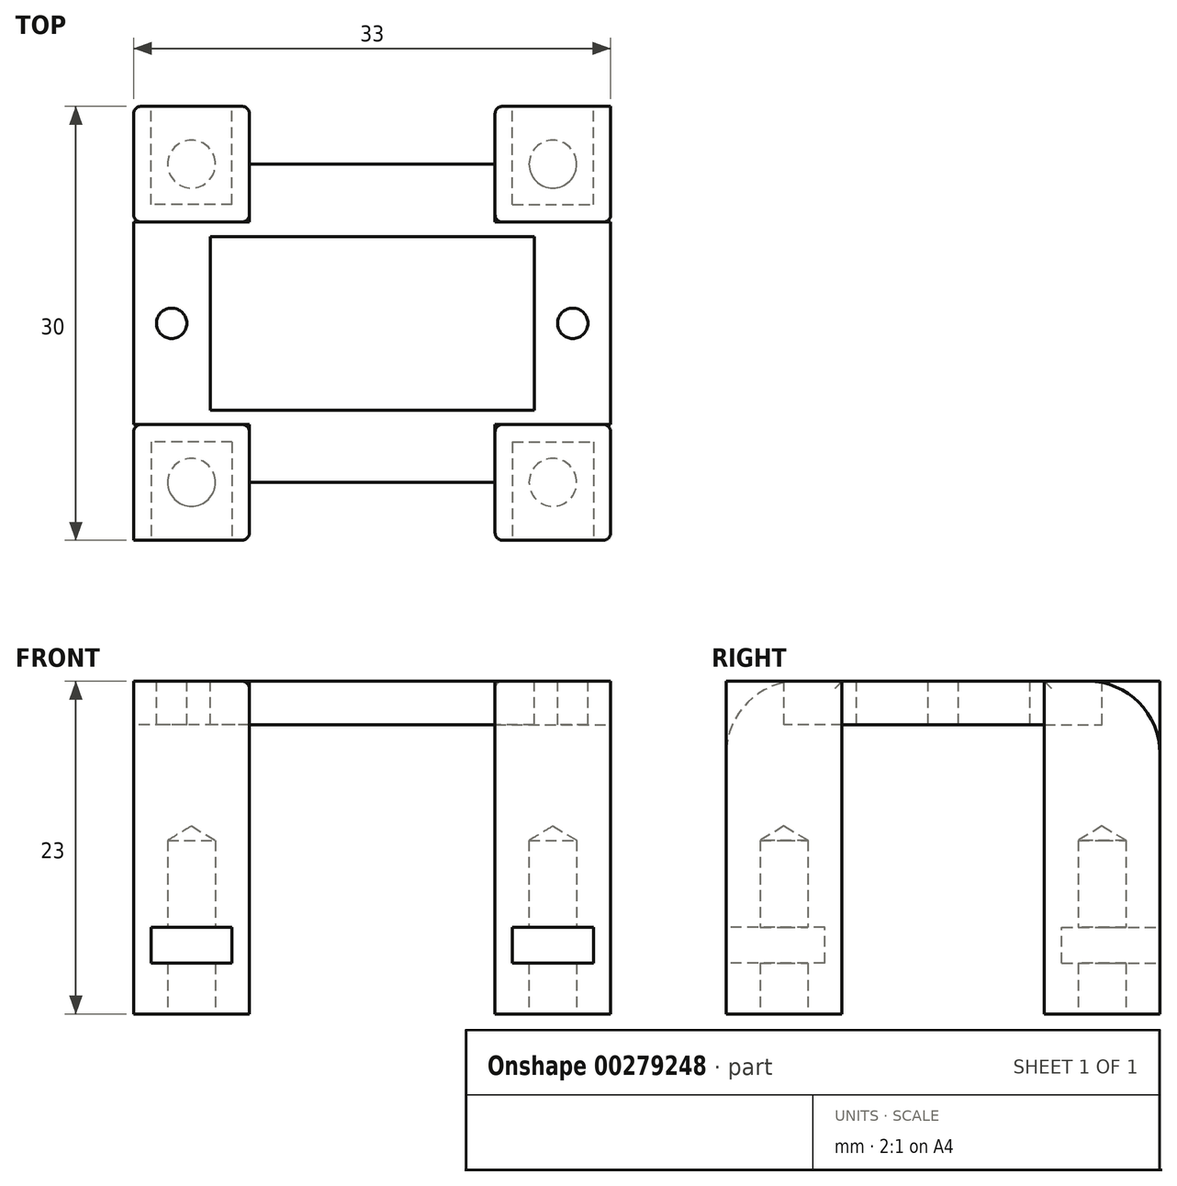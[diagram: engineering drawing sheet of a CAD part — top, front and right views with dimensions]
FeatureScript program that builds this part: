
annotation { "Feature Type Name" : "Feature", "Feature Type Description" : "" }
export const myFeature = defineFeature(function(context is Context, id is Id, definition is map)
    precondition{}
    {
        {
            var Q0;
            Q0=qCreatedBy(makeId("Top.planeOp"),FACE);
            var sketch = newSketch(context, id + "F0", { "sketchPlane" : qUnion([Q0])});
            skLineSegment(sketch, "E0.bottom", {"start": v(11.2, -6) * mm, "end": v(-11.2, -6) * mm});
            skLineSegment(sketch, "E0.top", {"start": v(11.2, 6) * mm, "end": v(-11.2, 6) * mm});
            skLineSegment(sketch, "E0.left", {"start": v(11.2, -6) * mm, "end": v(11.2, 6) * mm});
            skLineSegment(sketch, "E0.right", {"start": v(-11.2, -6) * mm, "end": v(-11.2, 6) * mm});
            skPoint(sketch, "E0.middle", {"position": v(0, 0) * mm});
            skLineSegment(sketch, "E1.bottom", {"start": v(16.5, -11) * mm, "end": v(-16.5, -11) * mm});
            skLineSegment(sketch, "E1.top", {"start": v(16.5, 11) * mm, "end": v(-16.5, 11) * mm});
            skLineSegment(sketch, "E1.left", {"start": v(16.5, -11) * mm, "end": v(16.5, 11) * mm});
            skLineSegment(sketch, "E1.right", {"start": v(-16.5, -11) * mm, "end": v(-16.5, 11) * mm});
            skCircle(sketch, "E2", {"center": v(-13.88, 0) * mm, "radius": 1.05 * mm});
            skCircle(sketch, "E3.MirrorC", {"center": v(13.88, 0) * mm, "radius": 1.05 * mm});
            skCircle(sketch, "E4", {"center": v(-12.5, 11) * mm, "radius": 1.57 * mm});
            skLineSegment(sketch, "E5.bottom", {"start": v(-8.5, 7) * mm, "end": v(-16.5, 7) * mm});
            skLineSegment(sketch, "E5.top", {"start": v(-8.5, 15) * mm, "end": v(-16.5, 15) * mm});
            skLineSegment(sketch, "E5.left", {"start": v(-8.5, 7) * mm, "end": v(-8.5, 15) * mm});
            skLineSegment(sketch, "E5.right", {"start": v(-16.5, 7) * mm, "end": v(-16.5, 15) * mm});
            skLineSegment(sketch, "E6.MirrorCS", {"start": v(16.5, 7) * mm, "end": v(16.5, 15) * mm});
            skLineSegment(sketch, "E7.MirrorCS", {"start": v(8.5, 7) * mm, "end": v(8.5, 15) * mm});
            skLineSegment(sketch, "E8.MirrorCS", {"start": v(8.5, 7) * mm, "end": v(16.5, 7) * mm});
            skLineSegment(sketch, "E9.MirrorCS", {"start": v(8.5, 15) * mm, "end": v(16.5, 15) * mm});
            skCircle(sketch, "E10.MirrorC", {"center": v(12.5, 11) * mm, "radius": 1.57 * mm});
            skLineSegment(sketch, "E11.MirrorCS", {"start": v(16.5, -7) * mm, "end": v(16.5, -15) * mm});
            skLineSegment(sketch, "E12.MirrorCS", {"start": v(8.5, -7) * mm, "end": v(16.5, -7) * mm});
            skLineSegment(sketch, "E13.MirrorCS", {"start": v(8.5, -15) * mm, "end": v(16.5, -15) * mm});
            skLineSegment(sketch, "E14.MirrorCS", {"start": v(8.5, -7) * mm, "end": v(8.5, -15) * mm});
            skCircle(sketch, "E15.MirrorC", {"center": v(12.5, -11) * mm, "radius": 1.57 * mm});
            skCircle(sketch, "E16.MirrorC", {"center": v(-12.5, -11) * mm, "radius": 1.57 * mm});
            skLineSegment(sketch, "E17.MirrorCS", {"start": v(-8.5, -7) * mm, "end": v(-16.5, -7) * mm});
            skLineSegment(sketch, "E18.MirrorCS", {"start": v(-8.5, -7) * mm, "end": v(-8.5, -15) * mm});
            skLineSegment(sketch, "E19.MirrorCS", {"start": v(-8.5, -15) * mm, "end": v(-16.5, -15) * mm});
            skLineSegment(sketch, "E20.MirrorCS", {"start": v(-16.5, -7) * mm, "end": v(-16.5, -15) * mm});
            skSolve(sketch);
        }
        {
            var Q0;
            {var subQ6=sQuery(id+"F0.wireOp",EDGE,"E5.top");Q0=makeQuery(id+"F0.imprint","IMPRINT",FACE,{"disambiguationData":[TD([[makeQuery(id+"F0.imprint","IMPRINT",EDGE,{"derivedFrom":subQ6}),1.0]])]});}
            var Q1;
            {var subQ0=sQuery(id+"F0.wireOp",EDGE,"E4");var subQ1=sQuery(id+"F0.wireOp",EDGE,"E1.top");var subQ2=makeQuery(id+"F0.imprint","INTERSECT",VERTEX,{"disambiguationData":[OD(0.0)],"derivedFrom":[subQ1,subQ0]});Q1=makeQuery(id+"F0.imprint","IMPRINT",FACE,{"disambiguationData":[TD([[makeQuery(id+"F0.imprint","IMPRINT",EDGE,{"disambiguationData":[TD([[subQ2,-1.0]])],"derivedFrom":subQ1}),-1.0]])]});}
            var Q2;
            {var subQ0=sQuery(id+"F0.wireOp",EDGE,"E4");var subQ1=sQuery(id+"F0.wireOp",EDGE,"E1.top");var subQ2=makeQuery(id+"F0.imprint","INTERSECT",VERTEX,{"disambiguationData":[OD(0.0)],"derivedFrom":[subQ1,subQ0]});Q2=makeQuery(id+"F0.imprint","IMPRINT",FACE,{"disambiguationData":[TD([[makeQuery(id+"F0.imprint","IMPRINT",EDGE,{"disambiguationData":[TD([[subQ2,-1.0]])],"derivedFrom":subQ1}),1.0]])]});}
            var Q3;
            {var subQ0=sQuery(id+"F0.wireOp",EDGE,"E5.bottom");Q3=makeQuery(id+"F0.imprint","IMPRINT",FACE,{"disambiguationData":[TD([[makeQuery(id+"F0.imprint","IMPRINT",EDGE,{"derivedFrom":subQ0}),-1.0]])]});}
            var Q4;
            {var subQ0=sQuery(id+"F0.wireOp",EDGE,"E9.MirrorCS");Q4=makeQuery(id+"F0.imprint","IMPRINT",FACE,{"disambiguationData":[TD([[makeQuery(id+"F0.imprint","IMPRINT",EDGE,{"derivedFrom":subQ0}),-1.0]])]});}
            var Q5;
            {var subQ0=sQuery(id+"F0.wireOp",EDGE,"E10.MirrorC");var subQ1=sQuery(id+"F0.wireOp",EDGE,"E1.top");var subQ2=makeQuery(id+"F0.imprint","INTERSECT",VERTEX,{"disambiguationData":[OD(0.0)],"derivedFrom":[subQ1,subQ0]});Q5=makeQuery(id+"F0.imprint","IMPRINT",FACE,{"disambiguationData":[TD([[makeQuery(id+"F0.imprint","IMPRINT",EDGE,{"disambiguationData":[TD([[subQ2,-1.0]])],"derivedFrom":subQ1}),-1.0]])]});}
            var Q6;
            {var subQ0=sQuery(id+"F0.wireOp",EDGE,"E10.MirrorC");var subQ1=sQuery(id+"F0.wireOp",EDGE,"E1.top");var subQ2=makeQuery(id+"F0.imprint","INTERSECT",VERTEX,{"disambiguationData":[OD(0.0)],"derivedFrom":[subQ1,subQ0]});Q6=makeQuery(id+"F0.imprint","IMPRINT",FACE,{"disambiguationData":[TD([[makeQuery(id+"F0.imprint","IMPRINT",EDGE,{"disambiguationData":[TD([[subQ2,-1.0]])],"derivedFrom":subQ1}),1.0]])]});}
            var Q7;
            {var subQ0=sQuery(id+"F0.wireOp",EDGE,"E8.MirrorCS");Q7=makeQuery(id+"F0.imprint","IMPRINT",FACE,{"disambiguationData":[TD([[makeQuery(id+"F0.imprint","IMPRINT",EDGE,{"derivedFrom":subQ0}),1.0]])]});}
            var Q8;
            {var subQ6=sQuery(id+"F0.wireOp",EDGE,"E17.MirrorCS");Q8=makeQuery(id+"F0.imprint","IMPRINT",FACE,{"disambiguationData":[TD([[makeQuery(id+"F0.imprint","IMPRINT",EDGE,{"derivedFrom":subQ6}),1.0]])]});}
            var Q9;
            {var subQ0=sQuery(id+"F0.wireOp",EDGE,"E16.MirrorC");var subQ1=sQuery(id+"F0.wireOp",EDGE,"E1.bottom");var subQ2=makeQuery(id+"F0.imprint","INTERSECT",VERTEX,{"disambiguationData":[OD(0.0)],"derivedFrom":[subQ1,subQ0]});Q9=makeQuery(id+"F0.imprint","IMPRINT",FACE,{"disambiguationData":[TD([[makeQuery(id+"F0.imprint","IMPRINT",EDGE,{"disambiguationData":[TD([[subQ2,-1.0]])],"derivedFrom":subQ1}),-1.0]])]});}
            var Q10;
            {var subQ0=sQuery(id+"F0.wireOp",EDGE,"E16.MirrorC");var subQ1=sQuery(id+"F0.wireOp",EDGE,"E1.bottom");var subQ2=makeQuery(id+"F0.imprint","INTERSECT",VERTEX,{"disambiguationData":[OD(0.0)],"derivedFrom":[subQ1,subQ0]});Q10=makeQuery(id+"F0.imprint","IMPRINT",FACE,{"disambiguationData":[TD([[makeQuery(id+"F0.imprint","IMPRINT",EDGE,{"disambiguationData":[TD([[subQ2,-1.0]])],"derivedFrom":subQ1}),1.0]])]});}
            var Q11;
            {var subQ4=sQuery(id+"F0.wireOp",EDGE,"E19.MirrorCS");Q11=makeQuery(id+"F0.imprint","IMPRINT",FACE,{"disambiguationData":[TD([[makeQuery(id+"F0.imprint","IMPRINT",EDGE,{"derivedFrom":subQ4}),-1.0]])]});}
            var Q12;
            {var subQ0=sQuery(id+"F0.wireOp",EDGE,"E15.MirrorC");var subQ1=sQuery(id+"F0.wireOp",EDGE,"E1.bottom");var subQ2=makeQuery(id+"F0.imprint","INTERSECT",VERTEX,{"disambiguationData":[OD(0.0)],"derivedFrom":[subQ1,subQ0]});Q12=makeQuery(id+"F0.imprint","IMPRINT",FACE,{"disambiguationData":[TD([[makeQuery(id+"F0.imprint","IMPRINT",EDGE,{"disambiguationData":[TD([[subQ2,-1.0]])],"derivedFrom":subQ1}),-1.0]])]});}
            var Q13;
            {var subQ0=sQuery(id+"F0.wireOp",EDGE,"E15.MirrorC");var subQ1=sQuery(id+"F0.wireOp",EDGE,"E1.bottom");var subQ2=makeQuery(id+"F0.imprint","INTERSECT",VERTEX,{"disambiguationData":[OD(0.0)],"derivedFrom":[subQ1,subQ0]});Q13=makeQuery(id+"F0.imprint","IMPRINT",FACE,{"disambiguationData":[TD([[makeQuery(id+"F0.imprint","IMPRINT",EDGE,{"disambiguationData":[TD([[subQ2,-1.0]])],"derivedFrom":subQ1}),1.0]])]});}
            var Q14;
            {var subQ0=sQuery(id+"F0.wireOp",EDGE,"E12.MirrorCS");Q14=makeQuery(id+"F0.imprint","IMPRINT",FACE,{"disambiguationData":[TD([[makeQuery(id+"F0.imprint","IMPRINT",EDGE,{"derivedFrom":subQ0}),-1.0]])]});}
            var Q15;
            {var subQ0=sQuery(id+"F0.wireOp",EDGE,"E13.MirrorCS");Q15=makeQuery(id+"F0.imprint","IMPRINT",FACE,{"disambiguationData":[TD([[makeQuery(id+"F0.imprint","IMPRINT",EDGE,{"derivedFrom":subQ0}),1.0]])]});}
            extrude(context, id + "F1", {"entities" : qUnion([Q0, Q1, Q2, Q3, Q4, Q5, Q6, Q7, Q8, Q9, Q10, Q11, Q12, Q13, Q14, Q15]), "oppositeDirection" : true, "depth" : 23 * mm});
        }
        {
            var Q0;
            Q0=makeQuery(id+"F0.imprint","IMPRINT",FACE,{"disambiguationData":[TD([[makeQuery(id+"F0.imprint","IMPRINT",EDGE,{"derivedFrom":sQuery(id+"F0.wireOp",EDGE,"E0.bottom")}),1.0]])]});
            extrude(context, id + "F2", {"entities" : qUnion([Q0]), "oppositeDirection" : true, "depth" : 3 * mm});
        }
        {
            var Q0;
            Q0=makeQuery(id+"F1.opExtrude","CAP_FACE",FACE,{"disambiguationData":[OSD([sQuery(id+"F0.wireOp",EDGE,"E5.bottom"),sQuery(id+"F0.wireOp",EDGE,"E5.top"),sQuery(id+"F0.wireOp",EDGE,"E5.left"),sQuery(id+"F0.wireOp",EDGE,"E5.right")])],"isStart":false});
            var sketch = newSketch(context, id + "F3", { "sketchPlane" : qUnion([Q0])});
            skCircle(sketch, "E21", {"center": v(-12.5, -11) * mm, "radius": 1.57 * mm});
            skCircle(sketch, "E22.MirrorC", {"center": v(12.5, -11) * mm, "radius": 1.57 * mm});
            skCircle(sketch, "E23.MirrorC", {"center": v(-12.5, 11) * mm, "radius": 1.57 * mm});
            skCircle(sketch, "E24.MirrorC", {"center": v(12.5, 11) * mm, "radius": 1.57 * mm});
            skLineSegment(sketch, "E25.bottom", {"start": v(-9.7, -8.2) * mm, "end": v(-15.3, -8.2) * mm});
            skLineSegment(sketch, "E25.top", {"start": v(-9.7, -13.8) * mm, "end": v(-15.3, -13.8) * mm});
            skLineSegment(sketch, "E25.left", {"start": v(-9.7, -8.2) * mm, "end": v(-9.7, -13.8) * mm});
            skLineSegment(sketch, "E25.right", {"start": v(-15.3, -8.2) * mm, "end": v(-15.3, -13.8) * mm});
            skSolve(sketch);
        }
        {
            var Q0;
            Q0=sQuery(id+"F3.wireOp",VERTEX,"E23.MirrorC.center");
            var Q1;
            Q1=sQuery(id+"F3.wireOp",VERTEX,"E24.MirrorC.center");
            var Q2;
            Q2=sQuery(id+"F3.wireOp",VERTEX,"E21.center");
            var Q3;
            Q3=sQuery(id+"F3.wireOp",VERTEX,"E22.MirrorC.center");
            var Q4;
            Q4=makeQuery(id+"F1.opExtrude","SWEPT_BODY",BODY,{"disambiguationData":[OSD([sQuery(id+"F0.wireOp",EDGE,"E17.MirrorCS"),sQuery(id+"F0.wireOp",EDGE,"E18.MirrorCS"),sQuery(id+"F0.wireOp",EDGE,"E19.MirrorCS"),sQuery(id+"F0.wireOp",EDGE,"E20.MirrorCS")])]});
            var Q5;
            Q5=makeQuery(id+"F1.opExtrude","SWEPT_BODY",BODY,{"disambiguationData":[OSD([sQuery(id+"F0.wireOp",EDGE,"E11.MirrorCS"),sQuery(id+"F0.wireOp",EDGE,"E12.MirrorCS"),sQuery(id+"F0.wireOp",EDGE,"E13.MirrorCS"),sQuery(id+"F0.wireOp",EDGE,"E14.MirrorCS")])]});
            var Q6;
            Q6=makeQuery(id+"F1.opExtrude","SWEPT_BODY",BODY,{"disambiguationData":[OSD([sQuery(id+"F0.wireOp",EDGE,"E5.bottom"),sQuery(id+"F0.wireOp",EDGE,"E5.top"),sQuery(id+"F0.wireOp",EDGE,"E5.left"),sQuery(id+"F0.wireOp",EDGE,"E5.right")])]});
            var Q7;
            Q7=makeQuery(id+"F1.opExtrude","SWEPT_BODY",BODY,{"disambiguationData":[OSD([sQuery(id+"F0.wireOp",EDGE,"E6.MirrorCS"),sQuery(id+"F0.wireOp",EDGE,"E7.MirrorCS"),sQuery(id+"F0.wireOp",EDGE,"E8.MirrorCS"),sQuery(id+"F0.wireOp",EDGE,"E9.MirrorCS")])]});
            hole(context, id + "F4", {"style" : HoleStyle.SIMPLE, "endStyle" : HoleEndStyle.BLIND, "standardTappedOrClearance" : lookupTablePath({ "standard" : "ISO", "fit" : "Normal", "size" : "M3", "type" : "Clearance" }), "standardBlindInLast" : lookupTablePath({ "fit" : "Standard", "standard" : "ISO", "size" : "M3", "type" : "Clearance" }), "holeDiameter" : 3.3 * mm, "holeDepth" : 12 * mm, "tappedDepth" : 12 * mm, "tapClearance" : 3, "locations" : qUnion([Q0, Q1, Q2, Q3]), "scope" : qUnion([Q4, Q5, Q6, Q7])});
        }
        {
            var Q0;
            Q0=makeQuery(id+"F1.opExtrude","SWEPT_FACE",FACE,{"disambiguationData":[OSD([sQuery(id+"F0.wireOp",EDGE,"E19.MirrorCS")])]});
            var sketch = newSketch(context, id + "F5", { "sketchPlane" : qUnion([Q0])});
            skLineSegment(sketch, "E26.bottom", {"start": v(-9.7, -19.5) * mm, "end": v(-15.3, -19.5) * mm});
            skLineSegment(sketch, "E26.top", {"start": v(-9.7, -17) * mm, "end": v(-15.3, -17) * mm});
            skLineSegment(sketch, "E26.left", {"start": v(-9.7, -19.5) * mm, "end": v(-9.7, -17) * mm});
            skLineSegment(sketch, "E26.right", {"start": v(-15.3, -19.5) * mm, "end": v(-15.3, -17) * mm});
            skPoint(sketch, "E26.middle", {"position": v(-12.5, -18.25) * mm});
            skLineSegment(sketch, "E27.MirrorCS", {"start": v(15.3, -19.5) * mm, "end": v(15.3, -17) * mm});
            skLineSegment(sketch, "E28.MirrorCS", {"start": v(9.7, -19.5) * mm, "end": v(9.7, -17) * mm});
            skLineSegment(sketch, "E29.MirrorCS", {"start": v(9.7, -19.5) * mm, "end": v(15.3, -19.5) * mm});
            skLineSegment(sketch, "E30.MirrorCS", {"start": v(9.7, -17) * mm, "end": v(15.3, -17) * mm});
            skPoint(sketch, "E31.MirrorP", {"position": v(12.5, -18.25) * mm});
            skSolve(sketch);
        }
        {
            var Q0;
            Q0=makeQuery(id+"F1.opExtrude","SWEPT_FACE",FACE,{"disambiguationData":[OSD([sQuery(id+"F0.wireOp",EDGE,"E9.MirrorCS")])]});
            var sketch = newSketch(context, id + "F6", { "sketchPlane" : qUnion([Q0])});
            skLineSegment(sketch, "E32.bottom", {"start": v(-9.7, -19.5) * mm, "end": v(-15.3, -19.5) * mm});
            skLineSegment(sketch, "E32.top", {"start": v(-9.7, -17) * mm, "end": v(-15.3, -17) * mm});
            skLineSegment(sketch, "E32.left", {"start": v(-9.7, -19.5) * mm, "end": v(-9.7, -17) * mm});
            skLineSegment(sketch, "E32.right", {"start": v(-15.3, -19.5) * mm, "end": v(-15.3, -17) * mm});
            skPoint(sketch, "E32.middle", {"position": v(-12.5, -18.25) * mm});
            skLineSegment(sketch, "E33.MirrorCS", {"start": v(9.7, -19.5) * mm, "end": v(15.3, -19.5) * mm});
            skLineSegment(sketch, "E34.MirrorCS", {"start": v(9.7, -17) * mm, "end": v(15.3, -17) * mm});
            skLineSegment(sketch, "E35.MirrorCS", {"start": v(15.3, -19.5) * mm, "end": v(15.3, -17) * mm});
            skLineSegment(sketch, "E36.MirrorCS", {"start": v(9.7, -19.5) * mm, "end": v(9.7, -17) * mm});
            skPoint(sketch, "E37.MirrorP", {"position": v(12.5, -18.25) * mm});
            skSolve(sketch);
        }
        {
            var Q0;
            Q0=makeQuery(id+"F5.imprint","IMPRINT",FACE,{"disambiguationData":[TD([[makeQuery(id+"F5.imprint","IMPRINT",EDGE,{"derivedFrom":sQuery(id+"F5.wireOp",EDGE,"E26.bottom")}),-1.0]])]});
            var Q1;
            Q1=makeQuery(id+"F5.imprint","IMPRINT",FACE,{"disambiguationData":[TD([[makeQuery(id+"F5.imprint","IMPRINT",EDGE,{"derivedFrom":sQuery(id+"F5.wireOp",EDGE,"E27.MirrorCS")}),1.0]])]});
            extrude(context, id + "F7", {"entities" : qUnion([Q0, Q1]), "operationType" : NewBodyOperationType.REMOVE, "oppositeDirection" : true, "depth" : 6.8 * mm});
        }
        {
            var Q0;
            Q0=makeQuery(id+"F6.imprint","IMPRINT",FACE,{"disambiguationData":[TD([[makeQuery(id+"F6.imprint","IMPRINT",EDGE,{"derivedFrom":sQuery(id+"F6.wireOp",EDGE,"E32.bottom")}),-1.0]])]});
            var Q1;
            Q1=makeQuery(id+"F6.imprint","IMPRINT",FACE,{"disambiguationData":[TD([[makeQuery(id+"F6.imprint","IMPRINT",EDGE,{"derivedFrom":sQuery(id+"F6.wireOp",EDGE,"E33.MirrorCS")}),1.0]])]});
            extrude(context, id + "F8", {"entities" : qUnion([Q0, Q1]), "operationType" : NewBodyOperationType.REMOVE, "oppositeDirection" : true, "depth" : 6.8 * mm});
        }
        {
            var Q0;
            Q0=makeQuery(id+"F1.opExtrude","CAP_EDGE",EDGE,{"disambiguationData":[OSD([sQuery(id+"F0.wireOp",EDGE,"E9.MirrorCS")])],"isStart":true});
            var Q1;
            Q1=makeQuery(id+"F1.opExtrude","CAP_EDGE",EDGE,{"disambiguationData":[OSD([sQuery(id+"F0.wireOp",EDGE,"E19.MirrorCS")])],"isStart":true});
            fillet(context, id + "F9", {"entities" : qUnion([Q0, Q1]), "radius" : 5 * mm, "tangentPropagation" : true, "allowEdgeOverflow" : false});
        }
        {
            var Q0;
            Q0=makeQuery(id+"F1.opExtrude","SWEPT_EDGE",EDGE,{"disambiguationData":[OSD([sQuery(id+"F0.wireOp",EDGE,"E11.MirrorCS"),sQuery(id+"F0.wireOp",EDGE,"E13.MirrorCS")])]});
            var Q1;
            Q1=makeQuery(id+"F1.opExtrude","SWEPT_EDGE",EDGE,{"disambiguationData":[OSD([sQuery(id+"F0.wireOp",EDGE,"E1.left"),sQuery(id+"F0.wireOp",EDGE,"E11.MirrorCS"),sQuery(id+"F0.wireOp",EDGE,"E12.MirrorCS")])]});
            var Q2;
            Q2=makeQuery(id+"F1.opExtrude","SWEPT_EDGE",EDGE,{"disambiguationData":[OSD([sQuery(id+"F0.wireOp",EDGE,"E18.MirrorCS"),sQuery(id+"F0.wireOp",EDGE,"E19.MirrorCS")])]});
            var Q3;
            Q3=makeQuery(id+"F1.opExtrude","SWEPT_EDGE",EDGE,{"disambiguationData":[OSD([sQuery(id+"F0.wireOp",EDGE,"E1.left"),sQuery(id+"F0.wireOp",EDGE,"E6.MirrorCS"),sQuery(id+"F0.wireOp",EDGE,"E8.MirrorCS")])]});
            var Q4;
            Q4=makeQuery(id+"F1.opExtrude","SWEPT_EDGE",EDGE,{"disambiguationData":[OSD([sQuery(id+"F0.wireOp",EDGE,"E5.top"),sQuery(id+"F0.wireOp",EDGE,"E5.right")])]});
            var Q5;
            Q5=makeQuery(id+"F1.opExtrude","SWEPT_EDGE",EDGE,{"disambiguationData":[OSD([sQuery(id+"F0.wireOp",EDGE,"E5.top"),sQuery(id+"F0.wireOp",EDGE,"E5.left")])]});
            var Q6;
            Q6=makeQuery(id+"F1.opExtrude","SWEPT_EDGE",EDGE,{"disambiguationData":[OSD([sQuery(id+"F0.wireOp",EDGE,"E7.MirrorCS"),sQuery(id+"F0.wireOp",EDGE,"E9.MirrorCS")])]});
            var Q7;
            Q7=makeQuery(id+"F1.opExtrude","SWEPT_EDGE",EDGE,{"disambiguationData":[OSD([sQuery(id+"F0.wireOp",EDGE,"E12.MirrorCS"),sQuery(id+"F0.wireOp",EDGE,"E14.MirrorCS")])]});
            var Q8;
            Q8=makeQuery(id+"F1.opExtrude","SWEPT_EDGE",EDGE,{"disambiguationData":[OSD([sQuery(id+"F0.wireOp",EDGE,"E7.MirrorCS"),sQuery(id+"F0.wireOp",EDGE,"E8.MirrorCS")])]});
            var Q9;
            Q9=makeQuery(id+"F1.opExtrude","SWEPT_EDGE",EDGE,{"disambiguationData":[OSD([sQuery(id+"F0.wireOp",EDGE,"E5.bottom"),sQuery(id+"F0.wireOp",EDGE,"E5.left")])]});
            var Q10;
            Q10=makeQuery(id+"F1.opExtrude","SWEPT_EDGE",EDGE,{"disambiguationData":[OSD([sQuery(id+"F0.wireOp",EDGE,"E17.MirrorCS"),sQuery(id+"F0.wireOp",EDGE,"E18.MirrorCS")])]});
            var Q11;
            Q11=makeQuery(id+"F1.opExtrude","SWEPT_EDGE",EDGE,{"disambiguationData":[OSD([sQuery(id+"F0.wireOp",EDGE,"E1.right"),sQuery(id+"F0.wireOp",EDGE,"E5.bottom"),sQuery(id+"F0.wireOp",EDGE,"E5.right")])]});
            var Q12;
            Q12=makeQuery(id+"F1.opExtrude","SWEPT_EDGE",EDGE,{"disambiguationData":[OSD([sQuery(id+"F0.wireOp",EDGE,"E1.right"),sQuery(id+"F0.wireOp",EDGE,"E17.MirrorCS"),sQuery(id+"F0.wireOp",EDGE,"E20.MirrorCS")])]});
            var Q13;
            Q13=makeQuery(id+"F1.opExtrude","SWEPT_EDGE",EDGE,{"disambiguationData":[OSD([sQuery(id+"F0.wireOp",EDGE,"E13.MirrorCS"),sQuery(id+"F0.wireOp",EDGE,"E14.MirrorCS")])]});
            fillet(context, id + "F10", {"entities" : qUnion([Q0, Q1, Q2, Q3, Q4, Q5, Q6, Q7, Q8, Q9, Q10, Q11, Q12, Q13]), "radius" : .5 * mm, "tangentPropagation" : true, "allowEdgeOverflow" : false});
        }
    });
